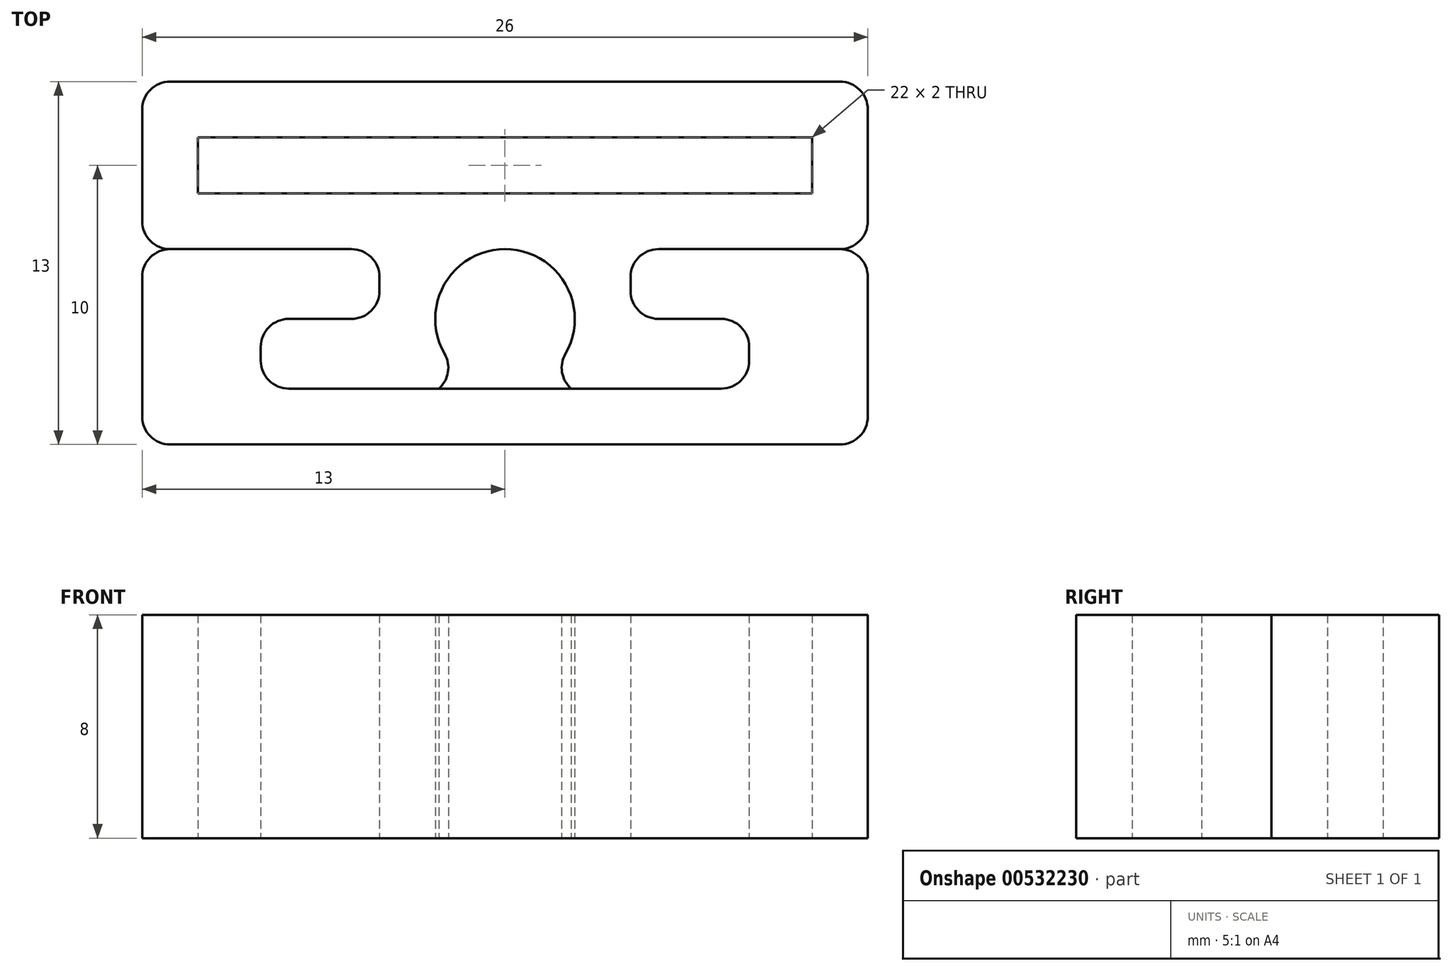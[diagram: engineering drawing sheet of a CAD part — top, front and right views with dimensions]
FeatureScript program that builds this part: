
annotation { "Feature Type Name" : "Feature", "Feature Type Description" : "" }
export const myFeature = defineFeature(function(context is Context, id is Id, definition is map)
    precondition{}
    {
        {
            var Q0;
            Q0=qCreatedBy(makeId("Top.planeOp"),FACE);
            var sketch = newSketch(context, id + "F0", { "sketchPlane" : qUnion([Q0])});
            skPoint(sketch, "E0.middle", {"position": v(0, 0) * mm});
            skLineSegment(sketch, "E1.0", {"start": v(12, 3) * mm, "end": v(-12, 3) * mm});
            skLineSegment(sketch, "E1.1", {"start": v(13, -2) * mm, "end": v(13, 2) * mm});
            skLineSegment(sketch, "E1.2", {"start": v(12, -3) * mm, "end": v(5.5, -3) * mm});
            skLineSegment(sketch, "E1.3", {"start": v(-13, -2) * mm, "end": v(-13, 2) * mm});
            skArc(sketch, "E2", {"start": v(2.17, -6.75) * mm, "mid": v(0, -3) * mm, "end": v(-2.17, -6.75) * mm});
            skPoint(sketch, "E2.centerSnap0", {"position": v(0, -3) * mm});
            skLineSegment(sketch, "E3.trimOffspring", {"start": v(-5.5, -3) * mm, "end": v(-12, -3) * mm});
            skLineSegment(sketch, "E4", {"start": v(-4.5, -4.5) * mm, "end": v(-4.5, -4) * mm});
            skLineSegment(sketch, "E5", {"start": v(4.5, -4.5) * mm, "end": v(4.5, -4) * mm});
            skPoint(sketch, "E6.visualSharp", {"position": v(-4.5, -3) * mm});
            skArc(sketch, "E6.filletArc", {"start": v(-4.5, -4) * mm, "mid": v(-4.8, -3.3) * mm, "end": v(-5.5, -3) * mm});
            skPoint(sketch, "E7.visualSharp", {"position": v(4.5, -3) * mm});
            skArc(sketch, "E7.filletArc", {"start": v(5.5, -3) * mm, "mid": v(4.8, -3.3) * mm, "end": v(4.5, -4) * mm});
            skPoint(sketch, "E8.visualSharp", {"position": v(13, -3) * mm});
            skArc(sketch, "E8.filletArc", {"start": v(12, -3) * mm, "mid": v(12.7, -2.7) * mm, "end": v(13, -2) * mm});
            skPoint(sketch, "E9.visualSharp", {"position": v(13, 3) * mm});
            skArc(sketch, "E9.filletArc", {"start": v(13, 2) * mm, "mid": v(12.7, 2.7) * mm, "end": v(12, 3) * mm});
            skPoint(sketch, "E10.visualSharp", {"position": v(-13, 3) * mm});
            skArc(sketch, "E10.filletArc", {"start": v(-12, 3) * mm, "mid": v(-12.7, 2.7) * mm, "end": v(-13, 2) * mm});
            skPoint(sketch, "E11.visualSharp", {"position": v(-13, -3) * mm});
            skArc(sketch, "E11.filletArc", {"start": v(-13, -2) * mm, "mid": v(-12.7, -2.7) * mm, "end": v(-12, -3) * mm});
            skPoint(sketch, "E0.bottom.end.orphan", {"position": v(-11, -1) * mm});
            skPoint(sketch, "E0.left.end.orphan", {"position": v(11, 1) * mm});
            skLineSegment(sketch, "E12.bottom", {"start": v(-11, 1) * mm, "end": v(11, 1) * mm});
            skLineSegment(sketch, "E12.top", {"start": v(-11, -1) * mm, "end": v(11, -1) * mm});
            skLineSegment(sketch, "E12.left", {"start": v(-11, 1) * mm, "end": v(-11, -1) * mm});
            skLineSegment(sketch, "E12.right", {"start": v(11, 1) * mm, "end": v(11, -1) * mm});
            skLineSegment(sketch, "E13", {"start": v(-8.75, -6.5) * mm, "end": v(-8.75, -7) * mm});
            skLineSegment(sketch, "E14", {"start": v(-5.5, -5.5) * mm, "end": v(-7.75, -5.5) * mm});
            skLineSegment(sketch, "E15", {"start": v(-2.37, -8) * mm, "end": v(-7.75, -8) * mm});
            skPoint(sketch, "E16.orphan", {"position": v(-8.75, -3) * mm});
            skArc(sketch, "E17.trimOffspring", {"start": v(-2.37, -8) * mm, "mid": v(-2.04, -7.41) * mm, "end": v(-2.17, -6.75) * mm});
            skPoint(sketch, "E18.start.orphan", {"position": v(-3.9, -7.75) * mm});
            skPoint(sketch, "E19.visualSharp", {"position": v(-4.5, -5.5) * mm});
            skArc(sketch, "E19.filletArc", {"start": v(-5.5, -5.5) * mm, "mid": v(-4.8, -5.2) * mm, "end": v(-4.5, -4.5) * mm});
            skPoint(sketch, "E20.visualSharp", {"position": v(-8.75, -5.5) * mm});
            skArc(sketch, "E20.filletArc", {"start": v(-7.75, -5.5) * mm, "mid": v(-8.46, -5.8) * mm, "end": v(-8.75, -6.5) * mm});
            skPoint(sketch, "E21.visualSharp", {"position": v(-8.75, -8) * mm});
            skArc(sketch, "E21.filletArc", {"start": v(-8.75, -7) * mm, "mid": v(-8.46, -7.7) * mm, "end": v(-7.75, -8) * mm});
            skLineSegment(sketch, "E22.MirrorCS", {"start": v(2.37, -8) * mm, "end": v(7.75, -8) * mm});
            skArc(sketch, "E23.MirrorCS", {"start": v(8.75, -7) * mm, "mid": v(8.46, -7.7) * mm, "end": v(7.75, -8) * mm});
            skLineSegment(sketch, "E24.MirrorCS", {"start": v(8.75, -6.5) * mm, "end": v(8.75, -7) * mm});
            skArc(sketch, "E25.MirrorCS", {"start": v(7.75, -5.5) * mm, "mid": v(8.46, -5.8) * mm, "end": v(8.75, -6.5) * mm});
            skLineSegment(sketch, "E26.MirrorCS", {"start": v(5.5, -5.5) * mm, "end": v(7.75, -5.5) * mm});
            skArc(sketch, "E27.MirrorCS", {"start": v(5.5, -5.5) * mm, "mid": v(4.8, -5.2) * mm, "end": v(4.5, -4.5) * mm});
            skArc(sketch, "E28.trimOffspring", {"start": v(2.37, -8) * mm, "mid": v(2.04, -7.41) * mm, "end": v(2.17, -6.75) * mm});
            skSolve(sketch);
        }
        {
            var Q0;
            Q0=makeQuery(id+"F0.imprint","IMPRINT",FACE,{"disambiguationData":[TD([[makeQuery(id+"F0.imprint","IMPRINT",EDGE,{"derivedFrom":sQuery(id+"F0.wireOp",EDGE,"E1.0")}),1.0]])]});
            extrude(context, id + "F1", {"entities" : qUnion([Q0]), "depth" : 8 * mm, "offsetDistance" : 25 * mm});
        }
        {
            var Q0;
            Q0=qCreatedBy(makeId("Top.planeOp"),FACE);
            var sketch = newSketch(context, id + "F2", { "sketchPlane" : qUnion([Q0])});
            skLineSegment(sketch, "E29.0.1", {"start": v(2.37, -8) * mm, "end": v(7.75, -8) * mm});
            skArc(sketch, "E29.0.2", {"start": v(7.75, -8) * mm, "mid": v(8.46, -7.7) * mm, "end": v(8.75, -7) * mm});
            skLineSegment(sketch, "E29.0.3", {"start": v(8.75, -7) * mm, "end": v(8.75, -6.5) * mm});
            skArc(sketch, "E29.0.4", {"start": v(8.75, -6.5) * mm, "mid": v(8.46, -5.8) * mm, "end": v(7.75, -5.5) * mm});
            skLineSegment(sketch, "E29.0.5", {"start": v(7.75, -5.5) * mm, "end": v(5.5, -5.5) * mm});
            skArc(sketch, "E29.0.6", {"start": v(5.5, -5.5) * mm, "mid": v(4.8, -5.2) * mm, "end": v(4.5, -4.5) * mm});
            skLineSegment(sketch, "E29.0.7", {"start": v(4.5, -4.5) * mm, "end": v(4.5, -4) * mm});
            skArc(sketch, "E29.0.8", {"start": v(4.5, -4) * mm, "mid": v(4.8, -3.3) * mm, "end": v(5.5, -3) * mm});
            skLineSegment(sketch, "E29.0.9", {"start": v(5.5, -3) * mm, "end": v(12, -3) * mm});
            skLineSegment(sketch, "E29.0.17", {"start": v(-12, -3) * mm, "end": v(-5.5, -3) * mm});
            skArc(sketch, "E29.0.18", {"start": v(-5.5, -3) * mm, "mid": v(-4.8, -3.3) * mm, "end": v(-4.5, -4) * mm});
            skLineSegment(sketch, "E29.0.19", {"start": v(-4.5, -4) * mm, "end": v(-4.5, -4.5) * mm});
            skArc(sketch, "E29.0.20", {"start": v(-4.5, -4.5) * mm, "mid": v(-4.8, -5.2) * mm, "end": v(-5.5, -5.5) * mm});
            skLineSegment(sketch, "E29.0.21", {"start": v(-5.5, -5.5) * mm, "end": v(-7.75, -5.5) * mm});
            skArc(sketch, "E29.0.22", {"start": v(-7.75, -5.5) * mm, "mid": v(-8.46, -5.8) * mm, "end": v(-8.75, -6.5) * mm});
            skLineSegment(sketch, "E29.0.23", {"start": v(-8.75, -6.5) * mm, "end": v(-8.75, -7) * mm});
            skArc(sketch, "E29.0.24", {"start": v(-8.75, -7) * mm, "mid": v(-8.46, -7.7) * mm, "end": v(-7.75, -8) * mm});
            skLineSegment(sketch, "E29.0.25", {"start": v(-7.75, -8) * mm, "end": v(-2.37, -8) * mm});
            skLineSegment(sketch, "E30", {"start": v(-13, -4) * mm, "end": v(-13, -9) * mm});
            skLineSegment(sketch, "E31", {"start": v(13, -4) * mm, "end": v(13, -9) * mm});
            skLineSegment(sketch, "E32", {"start": v(-12, -10) * mm, "end": v(12, -10) * mm});
            skLineSegment(sketch, "E33", {"start": v(-2.37, -8) * mm, "end": v(2.37, -8) * mm});
            skLineSegment(sketch, "E34", {"start": v(-12, -3) * mm, "end": v(-12, -3) * mm});
            skLineSegment(sketch, "E35", {"start": v(12, -3) * mm, "end": v(12, -3) * mm});
            skPoint(sketch, "E29.0.14.start.orphan", {"position": v(-12, 3) * mm});
            skPoint(sketch, "E29.0.15.start.orphan", {"position": v(-13, 2) * mm});
            skPoint(sketch, "E29.0.12.end.orphan", {"position": v(12, 3) * mm});
            skPoint(sketch, "E29.0.11.end.orphan", {"position": v(13, 2) * mm});
            skPoint(sketch, "E36.visualSharp", {"position": v(-13, -3) * mm});
            skArc(sketch, "E36.filletArc", {"start": v(-12, -3) * mm, "mid": v(-12.7, -3.3) * mm, "end": v(-13, -4) * mm});
            skPoint(sketch, "E37.visualSharp", {"position": v(-13, -10) * mm});
            skArc(sketch, "E37.filletArc", {"start": v(-13, -9) * mm, "mid": v(-12.7, -9.7) * mm, "end": v(-12, -10) * mm});
            skPoint(sketch, "E38.visualSharp", {"position": v(13, -10) * mm});
            skArc(sketch, "E38.filletArc", {"start": v(12, -10) * mm, "mid": v(12.7, -9.7) * mm, "end": v(13, -9) * mm});
            skPoint(sketch, "E39.visualSharp", {"position": v(13, -3) * mm});
            skArc(sketch, "E39.filletArc", {"start": v(13, -4) * mm, "mid": v(12.7, -3.3) * mm, "end": v(12, -3) * mm});
            skPoint(sketch, "E29.0.16.start.orphan", {"position": v(-13, -2) * mm});
            skPoint(sketch, "E29.0.10.end.orphan", {"position": v(13, -2) * mm});
            skPoint(sketch, "E29.0.27.start.orphan", {"position": v(-2.17, -6.75) * mm});
            skPoint(sketch, "E29.0.0.start.orphan", {"position": v(2.17, -6.75) * mm});
            skSolve(sketch);
        }
        {
            var Q0;
            Q0 = qSketchRegion(id + "F2", true);
            extrude(context, id + "F3", {"entities" : qUnion([Q0]), "depth" : 8 * mm, "offsetDistance" : 25 * mm});
        }
    });
